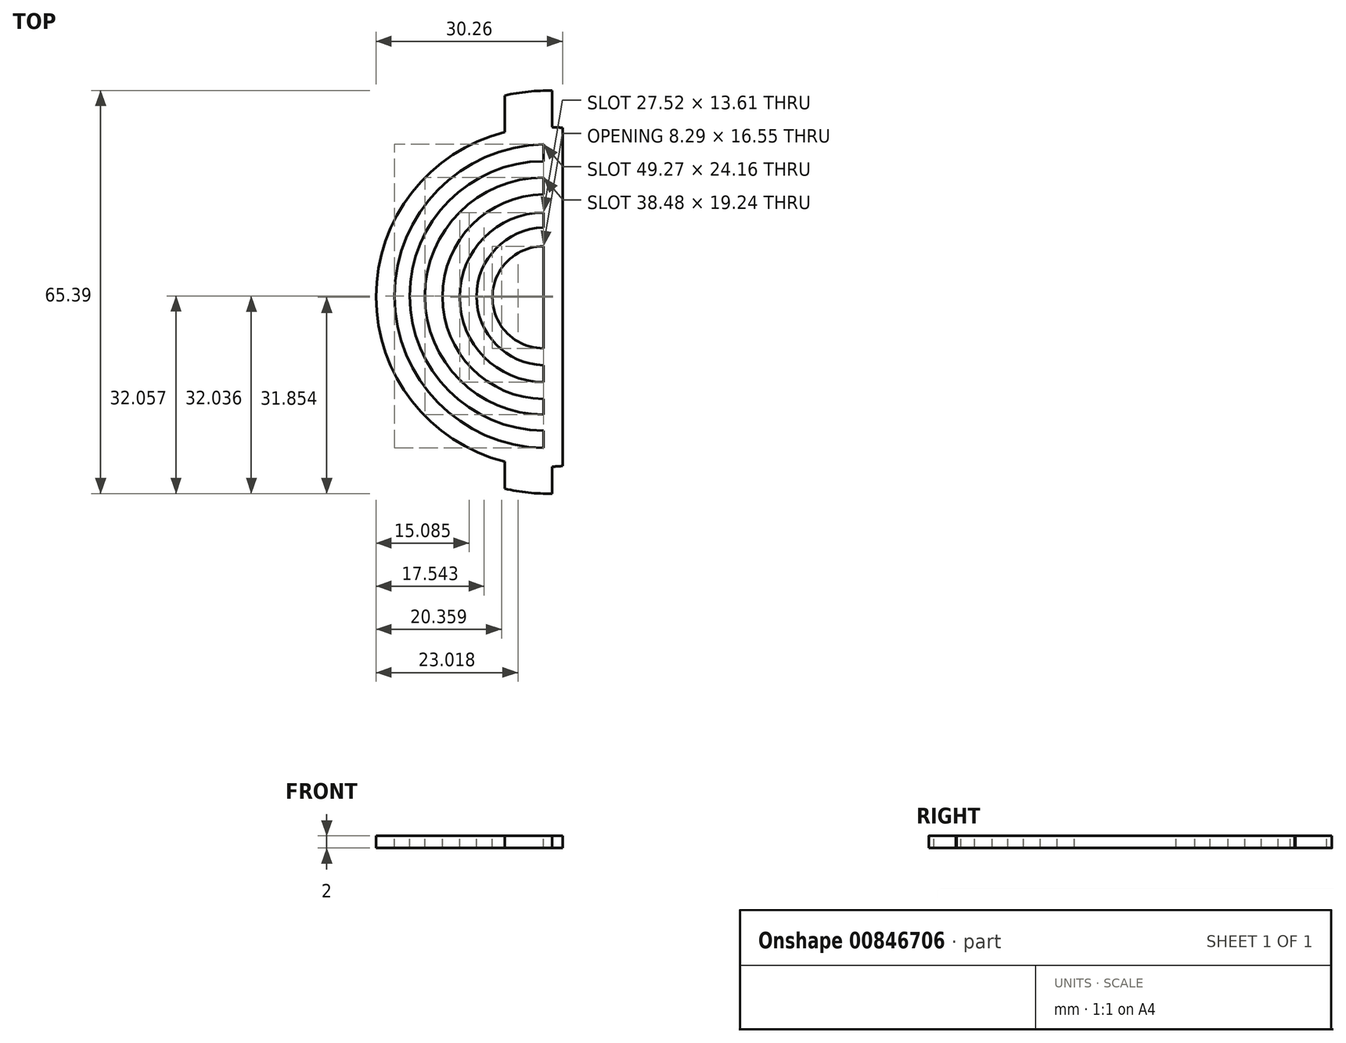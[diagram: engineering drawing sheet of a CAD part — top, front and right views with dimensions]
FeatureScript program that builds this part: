
annotation { "Feature Type Name" : "Feature", "Feature Type Description" : "" }
export const myFeature = defineFeature(function(context is Context, id is Id, definition is map)
    precondition{}
    {
        {
            var Q0;
            Q0=qCreatedBy(makeId("Top.planeOp"),FACE);
            var sketch = newSketch(context, id + "F0", { "sketchPlane" : qUnion([Q0])});
            skArc(sketch, "E0", {"start": v(-11.11, 45.9) * mm, "mid": v(-11.94, 45.98) * mm, "end": v(-12.77, 46.02) * mm});
            skLineSegment(sketch, "E1", {"start": v(-11.11, 45.9) * mm, "end": v(-11.11, -8.95) * mm});
            skLineSegment(sketch, "E2", {"start": v(-13.81, 18.48) * mm, "end": v(-50.05, 18.48) * mm, "construction": true});
            skArc(sketch, "E3", {"start": v(-12.77, 51.94) * mm, "mid": v(-16.66, 51.78) * mm, "end": v(-20.5, 51.15) * mm});
            skLineSegment(sketch, "E4", {"start": v(-12.77, 46.02) * mm, "end": v(-12.77, 51.94) * mm});
            skLineSegment(sketch, "E5", {"start": v(-20.5, 45.22) * mm, "end": v(-20.5, 51.15) * mm});
            skLineSegment(sketch, "E6", {"start": v(-20.5, -8.26) * mm, "end": v(-20.5, -12.65) * mm});
            skLineSegment(sketch, "E7", {"start": v(-12.77, -9.06) * mm, "end": v(-12.77, -13.44) * mm});
            skArc(sketch, "E8.trimOffspring", {"start": v(-20.5, -12.65) * mm, "mid": v(-16.66, -13.27) * mm, "end": v(-12.77, -13.44) * mm});
            skArc(sketch, "E9.trimOffspring", {"start": v(-20.5, 45.22) * mm, "mid": v(-41.37, 18.48) * mm, "end": v(-20.5, -8.26) * mm});
            skArc(sketch, "E10.trimOffspring", {"start": v(-12.77, -9.06) * mm, "mid": v(-11.94, -9.02) * mm, "end": v(-11.11, -8.95) * mm});
            skSolve(sketch);
        }
        {
            var Q0;
            Q0 = qSketchRegion(id + "F0", true);
            extrude(context, id + "F1", {"entities" : qUnion([Q0]), "oppositeDirection" : true, "depth" : 2 * mm, "offsetDistance" : 25 * mm});
        }
        {
            var Q0;
            Q0=qCreatedBy(makeId("Top.planeOp"),FACE);
            var sketch = newSketch(context, id + "F2", { "sketchPlane" : qUnion([Q0])});
            skArc(sketch, "E11", {"start": v(-14.2, 26.69) * mm, "mid": v(-22.5, 18.41) * mm, "end": v(-14.2, 10.14) * mm});
            skArc(sketch, "E12", {"start": v(-14.2, 32.17) * mm, "mid": v(-27.82, 18.41) * mm, "end": v(-14.2, 4.65) * mm});
            skArc(sketch, "E13", {"start": v(-14.2, 29.74) * mm, "mid": v(-25.07, 18.57) * mm, "end": v(-14.2, 7.4) * mm});
            skArc(sketch, "E14", {"start": v(-14.2, 35.12) * mm, "mid": v(-30.6, 18.52) * mm, "end": v(-14.2, 1.91) * mm});
            skArc(sketch, "E15", {"start": v(-14.2, 37.86) * mm, "mid": v(-33.45, 18.62) * mm, "end": v(-14.2, -0.63) * mm});
            skArc(sketch, "E16", {"start": v(-14.2, 40.5) * mm, "mid": v(-35.92, 18.65) * mm, "end": v(-14.2, -3.2) * mm});
            skArc(sketch, "E17", {"start": v(-14.2, 43.23) * mm, "mid": v(-38.36, 18.6) * mm, "end": v(-14.2, -6.04) * mm});
            skLineSegment(sketch, "E18", {"start": v(-14.2, 43.23) * mm, "end": v(-14.2, 40.5) * mm});
            skLineSegment(sketch, "E19", {"start": v(-14.2, 37.86) * mm, "end": v(-14.2, 35.12) * mm});
            skLineSegment(sketch, "E20", {"start": v(-14.2, 32.17) * mm, "end": v(-14.2, 29.74) * mm});
            skLineSegment(sketch, "E21", {"start": v(-14.2, 26.69) * mm, "end": v(-14.2, 10.14) * mm});
            skLineSegment(sketch, "E22", {"start": v(-14.2, 7.4) * mm, "end": v(-14.2, 4.65) * mm});
            skLineSegment(sketch, "E23", {"start": v(-14.2, 1.91) * mm, "end": v(-14.2, -0.63) * mm});
            skLineSegment(sketch, "E24", {"start": v(-14.2, -3.2) * mm, "end": v(-14.2, -6.04) * mm});
            skSolve(sketch);
        }
        {
            var Q0;
            Q0 = qSketchRegion(id + "F2", true);
            extrude(context, id + "F3", {"entities" : qUnion([Q0]), "operationType" : NewBodyOperationType.REMOVE, "oppositeDirection" : true, "depth" : 4 * mm, "offsetDistance" : 25 * mm});
        }
    });
